# Revit family: Overhead-Doors_400HP-Series_ASTA-America
name_source: partatom
category: Doors
units: mm (PartAtom-declared; Revit-internal decimal feet)

## family parameters
Always vertical = Yes
Classification Number = 23.30.10.00
Cut with Voids When Loaded = No
Host = Wall
Room Calculation Point = No
Shared = No

## types (1)
- Overhead-Doors_400HP-Series_ASTA-America
    Analytic Construction = <None>
    CAD Details = https://www.arcat.com
    Define Thermal Properties by = Schematic Type
    Description = ASTA AMERICA 400 Series Commercial Slat Doors
    Frame Projection Ext. = 0' - 1"
    Frame Projection Int. = 0' - 1"
    Frame Width = 0' - 3"
    Function = Interior
    Height = 15' - 0"
    Keynote = 08 33 00
    Manufacturer = ASTA America
    Model = 400HP
    Product Page URL = https://www.arcat.com
    Specification = https://www.arcat.com
    URL = https://www.astaamerica.com
    Wall Closure = By host
    Width = 10' - 0"
    Z_Chain Leght = 13' - 0"
    v = 0' - 0"
    x = 0' - 0"
    z_A1 = 0' - 0"
    z_A2 = 0' - 0"
    z_Bottom Profile = 0' - 0"
    z_Chain = Yes
    z_Commercial Operator = No
    z_Curved Array Height = 0' - 0"
    z_Height Control = 15' - 0"
    z_Leg Out Height = 15' - 11"
    z_Motor Width = 10' - 2 1/4"
    z_Offset = 0' - 0"
    z_Part Slat Number = 0
    z_Slat Door2 = Yes
    z_Slat Height = 0' - 2 21/32"
    z_Slat Number = 68
    z_Slat Offset = 4' - 4 7/8"
    z_Slat Width = 10' - 4"
    z_Structural Steel Guide = 0' - 0"
    z_Structural Steel Guide Visibility = Yes
    z_Third Array Height = 0' - 0"
    z_Width Control = 10' - 0"

## geometry (parser evidence)
native form markers: Sweep x10
no freeform markers — native parametric forms only
